FCSTD DOCUMENT  (FreeCAD 0.21R33771 (Git))
Label: Model_3
License: All rights reserved
LicenseURL: http://en.wikipedia.org/wiki/All_rights_reserved
objects: Sketcher::SketchObject×2, App::FeaturePython×2, Spreadsheet::Sheet×1, App::DocumentObjectGroupPython×1
note: 2 computed .brp shape members not serialized (recipe doc carries the construction recipe); baked Part::Feature solids carry a one-line shape summary decoded from their .brp

FEATURE [Spreadsheet::Sheet] Spreadsheet  label="Parametry"
  cells = A1='Parametry palca pacjenta, wartości proszę wpisywać w milimetrach; A3='Średnica palca pacjenta; B3='Średnica palca; C3(Srednica)=20; A4='Odległość od pierwszego więzadła do trzeciego więzadła palca pacjenta; B4='Długość paliczków; C4(Dlugosc)=60
FEATURE [Sketcher::SketchObject] Sketch  label="Model_cięcia"
  FullyConstrained = true
  expr: Constraints[103] = <<Parametry>>.Srednica
  expr: Constraints[104] = <<Parametry>>.Srednica
  expr: Constraints[105] = <<Parametry>>.Srednica
  expr: Constraints[106] = <<Parametry>>.Srednica
  expr: Constraints[107] = <<Parametry>>.Srednica / 2
  expr: Constraints[108] = <<Parametry>>.Srednica / 2
  expr: Constraints[109] = <<Parametry>>.Srednica / 2
  expr: Constraints[110] = <<Parametry>>.Srednica / 2
  expr: Constraints[12] = <<Parametry>>.Srednica
  expr: Constraints[131] = 0.5 * <<Parametry>>.Dlugosc + 0.5 * <<Parametry>>.Srednica
  expr: Constraints[132] = <<Parametry>>.Srednica / 2 + 8.5
  expr: Constraints[133] = <<Parametry>>.Srednica / 2
  expr: Constraints[134] = <<Parametry>>.Srednica / 2
  expr: Constraints[135] = <<Parametry>>.Srednica / 2
  expr: Constraints[136] = <<Parametry>>.Srednica / 2
  expr: Constraints[137] = <<Parametry>>.Srednica / 2
  expr: Constraints[138] = <<Parametry>>.Srednica / 2
  expr: Constraints[139] = <<Parametry>>.Srednica / 2
  expr: Constraints[13] = <<Parametry>>.Srednica
  expr: Constraints[140] = <<Parametry>>.Srednica / 2
  expr: Constraints[145] = 0.5 * <<Parametry>>.Dlugosc + 0.5 * <<Parametry>>.Srednica
  expr: Constraints[146] = <<Parametry>>.Srednica / 2 + 8.5
  expr: Constraints[14] = <<Parametry>>.Srednica
  expr: Constraints[15] = <<Parametry>>.Srednica
  expr: Constraints[20] = <<Parametry>>.Srednica
  expr: Constraints[21] = <<Parametry>>.Srednica
  expr: Constraints[22] = <<Parametry>>.Srednica
  expr: Constraints[23] = <<Parametry>>.Srednica
  expr: Constraints[24] = <<Parametry>>.Srednica
  expr: Constraints[25] = <<Parametry>>.Srednica
  expr: Constraints[26] = <<Parametry>>.Srednica
  expr: Constraints[27] = <<Parametry>>.Srednica
  expr: Constraints[83] = 0.5 * <<Parametry>>.Dlugosc + 0.5 * <<Parametry>>.Srednica
  expr: Constraints[84] = <<Parametry>>.Srednica / 2 + 8.5
  expr: Constraints[85] = <<Parametry>>.Srednica / 2
  expr: Constraints[86] = <<Parametry>>.Srednica / 2
  expr: Constraints[87] = <<Parametry>>.Srednica / 2
  expr: Constraints[88] = <<Parametry>>.Srednica / 2
  expr: Constraints[92] = <<Parametry>>.Dlugosc + 2 + <<Parametry>>.Srednica
  expr: Constraints[93] = <<Parametry>>.Srednica / 2 + 8.5
  expr: Constraints[94] = 0.5 * <<Parametry>>.Dlugosc + 0.5 * <<Parametry>>.Srednica
  expr: Constraints[9] = 2 * (<<Parametry>>.Srednica + 3) + 4 * 7 + 4
  sketch-geometry (56):
    g0: LineSegment StartX=0 StartY=0 StartZ=0 EndX=162 EndY=0 EndZ=0
    g1: LineSegment StartX=162 StartY=0 StartZ=0 EndX=162 EndY=78 EndZ=0
    g2: LineSegment StartX=162 StartY=78 StartZ=0 EndX=0 EndY=78 EndZ=0
    g3: LineSegment StartX=0 StartY=78 StartZ=0 EndX=0 EndY=0 EndZ=0
    g4: LineSegment StartX=30 StartY=18.5 StartZ=0 EndX=50 EndY=18.5 EndZ=0
    g5: LineSegment StartX=40 StartY=28.5 StartZ=0 EndX=40 EndY=8.5 EndZ=0
    g6: LineSegment StartX=32.9289 StartY=25.5711 StartZ=0 EndX=47.0711 EndY=11.4289 EndZ=0
    g7: LineSegment StartX=32.9289 StartY=11.4289 StartZ=0 EndX=47.0711 EndY=25.5711 EndZ=0
    g8: LineSegment StartX=30 StartY=59.5 StartZ=0 EndX=50 EndY=59.5 EndZ=0
    g9: LineSegment StartX=40 StartY=49.5 StartZ=0 EndX=40 EndY=69.5 EndZ=0
    g10: LineSegment StartX=32.9289 StartY=66.5711 StartZ=0 EndX=47.0711 EndY=52.4289 EndZ=0
    g11: LineSegment StartX=32.9289 StartY=52.4289 StartZ=0 EndX=47.0711 EndY=66.5711 EndZ=0
    g12: LineSegment StartX=112 StartY=59.5 StartZ=0 EndX=132 EndY=59.5 EndZ=0
    g13: LineSegment StartX=122 StartY=69.5 StartZ=0 EndX=122 EndY=49.5 EndZ=0
    g14: LineSegment StartX=114.929 StartY=66.5711 StartZ=0 EndX=129.071 EndY=52.4289 EndZ=0
    g15: LineSegment StartX=114.929 StartY=52.4289 StartZ=0 EndX=129.071 EndY=66.5711 EndZ=0
    g16: Circle CenterX=122 CenterY=49.5 CenterZ=0 NormalX=0 NormalY=0 NormalZ=1 AngleXU=0 Radius=0.25
    g17: Circle CenterX=114.929 CenterY=52.4289 CenterZ=0 NormalX=0 NormalY=0 NormalZ=1 AngleXU=0 Radius=0.25
    g18: Circle CenterX=112 CenterY=59.5 CenterZ=0 NormalX=0 NormalY=0 NormalZ=1 AngleXU=0 Radius=0.25
    g19: Circle CenterX=114.929 CenterY=66.5711 CenterZ=0 NormalX=0 NormalY=0 NormalZ=1 AngleXU=0 Radius=0.25
    g20: Circle CenterX=122 CenterY=69.5 CenterZ=0 NormalX=0 NormalY=0 NormalZ=1 AngleXU=0 Radius=0.25
    g21: Circle CenterX=129.071 CenterY=66.5711 CenterZ=0 NormalX=0 NormalY=0 NormalZ=1 AngleXU=0 Radius=0.25
    g22: Circle CenterX=132 CenterY=59.5 CenterZ=0 NormalX=0 NormalY=0 NormalZ=1 AngleXU=0 Radius=0.25
    g23: Circle CenterX=129.071 CenterY=52.4289 CenterZ=0 NormalX=0 NormalY=0 NormalZ=1 AngleXU=0 Radius=0.25
    g24: Circle CenterX=40 CenterY=69.5 CenterZ=0 NormalX=0 NormalY=0 NormalZ=1 AngleXU=0 Radius=0.25
    g25: Circle CenterX=47.0711 CenterY=66.5711 CenterZ=0 NormalX=0 NormalY=0 NormalZ=1 AngleXU=0 Radius=0.25
    g26: Circle CenterX=50 CenterY=59.5 CenterZ=0 NormalX=0 NormalY=0 NormalZ=1 AngleXU=0 Radius=0.25
    g27: Circle CenterX=47.0711 CenterY=52.4289 CenterZ=0 NormalX=0 NormalY=0 NormalZ=1 AngleXU=0 Radius=0.25
    g28: Circle CenterX=40 CenterY=49.5 CenterZ=0 NormalX=0 NormalY=0 NormalZ=1 AngleXU=0 Radius=0.25
    g29: Circle CenterX=32.9289 CenterY=52.4289 CenterZ=0 NormalX=0 NormalY=0 NormalZ=1 AngleXU=0 Radius=0.25
    g30: Circle CenterX=30 CenterY=59.5 CenterZ=0 NormalX=0 NormalY=0 NormalZ=1 AngleXU=0 Radius=0.25
    g31: Circle CenterX=32.9289 CenterY=66.5711 CenterZ=0 NormalX=0 NormalY=0 NormalZ=1 AngleXU=0 Radius=0.25
    g32: Circle CenterX=32.9289 CenterY=25.5711 CenterZ=0 NormalX=0 NormalY=0 NormalZ=1 AngleXU=0 Radius=0.25
    g33: Circle CenterX=30 CenterY=18.5 CenterZ=0 NormalX=0 NormalY=0 NormalZ=1 AngleXU=0 Radius=0.25
    g34: Circle CenterX=32.9289 CenterY=11.4289 CenterZ=0 NormalX=0 NormalY=0 NormalZ=1 AngleXU=0 Radius=0.25
    g35: Circle CenterX=47.0711 CenterY=11.4289 CenterZ=0 NormalX=0 NormalY=0 NormalZ=1 AngleXU=0 Radius=0.25
    g36: Circle CenterX=50 CenterY=18.5 CenterZ=0 NormalX=0 NormalY=0 NormalZ=1 AngleXU=0 Radius=0.25
    g37: Circle CenterX=47.0711 CenterY=25.5711 CenterZ=0 NormalX=0 NormalY=0 NormalZ=1 AngleXU=0 Radius=0.25
    g38: Circle CenterX=40 CenterY=8.5 CenterZ=0 NormalX=0 NormalY=0 NormalZ=1 AngleXU=0 Radius=0.25
    g39: Circle CenterX=40 CenterY=28.5 CenterZ=0 NormalX=0 NormalY=0 NormalZ=1 AngleXU=0 Radius=0.25
    g40: GeomPoint X=40 Y=18.5 Z=0
    g41: GeomPoint X=122 Y=18.5 Z=0
    g42: LineSegment StartX=114.929 StartY=11.4289 StartZ=0 EndX=129.071 EndY=25.5711 EndZ=0
    g43: LineSegment StartX=114.929 StartY=25.5711 StartZ=0 EndX=129.071 EndY=11.4289 EndZ=0
    g44: LineSegment StartX=122 StartY=28.5 StartZ=0 EndX=122 EndY=8.5 EndZ=0
    g45: LineSegment StartX=112 StartY=18.5 StartZ=0 EndX=132 EndY=18.5 EndZ=0
    g46: Circle CenterX=122 CenterY=28.5 CenterZ=0 NormalX=0 NormalY=0 NormalZ=1 AngleXU=0 Radius=0.25
    g47: Circle CenterX=129.071 CenterY=25.5711 CenterZ=0 NormalX=0 NormalY=0 NormalZ=1 AngleXU=0 Radius=0.25
    g48: Circle CenterX=132 CenterY=18.5 CenterZ=0 NormalX=0 NormalY=0 NormalZ=1 AngleXU=0 Radius=0.25
    g49: Circle CenterX=129.071 CenterY=11.4289 CenterZ=0 NormalX=0 NormalY=0 NormalZ=1 AngleXU=0 Radius=0.25
    g50: Circle CenterX=114.929 CenterY=11.4289 CenterZ=0 NormalX=0 NormalY=0 NormalZ=1 AngleXU=0 Radius=0.25
    g51: Circle CenterX=112 CenterY=18.5 CenterZ=0 NormalX=0 NormalY=0 NormalZ=1 AngleXU=0 Radius=0.25
    g52: Circle CenterX=114.929 CenterY=25.5711 CenterZ=0 NormalX=0 NormalY=0 NormalZ=1 AngleXU=0 Radius=0.25
    g53: Circle CenterX=122 CenterY=8.5 CenterZ=0 NormalX=0 NormalY=0 NormalZ=1 AngleXU=0 Radius=0.25
    g54: GeomPoint X=122 Y=59.5 Z=0
    g55: GeomPoint X=40 Y=59.5 Z=0
  constraints (147):
    c: Coincident(g0,g1)
    c: Coincident(g1,g2)
    c: Coincident(g2,g3)
    c: Coincident(g3,g0)
    c: Horizontal(g0)
    c: Horizontal(g2)
    c: Vertical(g1)
    c: Vertical(g3)
    c: Coincident(g0,g-1)
    c: DistanceY(g1,g1) = 78
    c: Horizontal(g4)
    c: Vertical(g5)
    c: DistanceX(g4,g4) = 20
    c: Distance(g7) = 20
    c: Distance(g5) = 20
    c: Distance(g6) = 20
    c: Angle(g4,g7) = 0.785398
    c: Angle(g6,g4) = 0.785398
    c: Horizontal(g8)
    c: Vertical(g9)
    c: Distance(g8) = 20
    c: Distance(g10) = 20
    c: Distance(g9) = 20
    c: Distance(g11) = 20
    c: Distance(g12) = 20
    c: Distance(g15) = 20
    c: Distance(g13) = 20
    c: Distance(g14) = 20
    c: Angle(g8,g11) = 0.785398
    c: Angle(g9,g10) = 0.785398
    c: Angle(g2,g12) = 0
    c: Angle(g2,g13) = 1.5708
    c: Angle(g12,g15) = 0.785398
    c: Angle(g14,g12) = 0.785398
    c: Coincident(g16,g13)
    c: Coincident(g17,g15)
    c: Coincident(g18,g12)
    c: Coincident(g19,g14)
    c: Coincident(g20,g13)
    c: Coincident(g21,g15)
    c: Coincident(g22,g12)
    c: Coincident(g23,g14)
    c: Coincident(g24,g9)
    c: Coincident(g25,g11)
    c: Coincident(g26,g8)
    c: Coincident(g27,g10)
    c: Coincident(g28,g9)
    c: Coincident(g29,g11)
    c: Coincident(g30,g8)
    c: Coincident(g31,g10)
    c: Coincident(g32,g6)
    c: Coincident(g33,g4)
    c: Coincident(g34,g7)
    c: Coincident(g35,g6)
    c: Coincident(g36,g4)
    c: Coincident(g37,g7)
    c: Coincident(g38,g5)
    c: Diameter(g30) = 0.5
    c: Diameter(g31) = 0.5
    c: Diameter(g24) = 0.5
    c: Diameter(g25) = 0.5
    c: Diameter(g26) = 0.5
    c: Diameter(g27) = 0.5
    c: Diameter(g28) = 0.5
    c: Diameter(g19) = 0.5
    c: Diameter(g20) = 0.5
    c: Diameter(g21) = 0.5
    c: Diameter(g22) = 0.5
    c: Diameter(g23) = 0.5
    c: Diameter(g16) = 0.5
    c: Diameter(g17) = 0.5
    c: Diameter(g18) = 0.5
    c: Diameter(g38) = 0.5
    c: Diameter(g35) = 0.5
    c: Diameter(g36) = 0.5
    c: Diameter(g37) = 0.5
    c: Diameter(g32) = 0.5
    c: Diameter(g33) = 0.5
    c: Diameter(g34) = 0.5
    c: Diameter(g29) = 0.5
    c: Coincident(g39,g5)
    c: Diameter(g39) = 0.5
    c: PointOnObject(g40,g4)
    c: DistanceX(g0,g40) = 40
    c: DistanceY(g0,g40) = 18.5
    c: Distance(g40,g4) = 10
    c: Distance(g40,g7) = 10
    c: Distance(g40,g6) = 10
    c: Distance(g40,g5) = 10
    c: PointOnObject(g40,g7)
    c: PointOnObject(g40,g6)
    c: PointOnObject(g40,g5)
    c: DistanceX(g40,g41) = 82
    c: DistanceY(g0,g41) = 18.5
    c: DistanceX(g41,g0) = 40
    c: PointOnObject(g41,g43)
    c: PointOnObject(g41,g42)
    c: PointOnObject(g41,g45)
    c: PointOnObject(g41,g44)
    c: Angle(g0,g45) = 0
    c: Angle(g44,g0) = 1.5708
    c: Angle(g42,g44) = 0.785398
    c: Angle(g44,g43) = 0.785398
    c: Distance(g43) = 20
    c: Distance(g42) = 20
    c: Distance(g44) = 20
    c: Distance(g45) = 20
    c: Distance(g41,g45) = 10
    c: Distance(g41,g42) = 10
    c: Distance(g41,g44) = 10
    c: Distance(g41,g43) = 10
    c: Coincident(g46,g44)
    c: Coincident(g47,g42)
    c: Coincident(g48,g45)
    c: Coincident(g49,g43)
    c: Coincident(g50,g42)
    c: Coincident(g51,g45)
    c: Coincident(g52,g43)
    c: Coincident(g53,g44)
    c: Diameter(g52) = 0.5
    c: Diameter(g46) = 0.5
    c: Diameter(g47) = 0.5
    c: Diameter(g48) = 0.5
    c: Diameter(g49) = 0.5
    c: Diameter(g53) = 0.5
    c: Diameter(g50) = 0.5
    c: Diameter(g51) = 0.5
    c: PointOnObject(g54,g13)
    c: PointOnObject(g54,g15)
    c: PointOnObject(g54,g12)
    c: PointOnObject(g54,g14)
    c: DistanceX(g54,g1) = 40
    c: DistanceY(g54,g1) = 18.5
    c: Distance(g54,g13) = 10
    c: Distance(g54,g15) = 10
    c: Distance(g54,g12) = 10
    c: Distance(g54,g14) = 10
    c: Distance(g55,g9) = 10
    c: Distance(g55,g11) = 10
    c: Distance(g55,g8) = 10
    c: Distance(g55,g10) = 10
    c: PointOnObject(g55,g10)
    c: PointOnObject(g55,g9)
    c: PointOnObject(g55,g11)
    c: PointOnObject(g55,g8)
    c: DistanceX(g2,g55) = 40
    c: DistanceY(g55,g2) = 18.5
FEATURE [App::FeaturePython] Layer  label="Cięcie laserem"  # WARN: FeaturePython — macro-defined, semantics opaque (R4)
  Group = -> [Sketch]
FEATURE [Sketcher::SketchObject] Sketch001  label="Model_zgrzewania"
  FullyConstrained = true
  expr: Constraints[10] = <<Parametry>>.Dlugosc + 2 + <<Parametry>>.Srednica
  expr: Constraints[11] = <<Parametry>>.Srednica / 2 + 8.5
  expr: Constraints[12] = <<Parametry>>.Srednica / 2 + 8.5
  expr: Constraints[13] = (2 * (<<Parametry>>.Srednica + 3) + 4 * 7 + 4) * 0.5
  expr: Constraints[14] = (2 * (<<Parametry>>.Srednica + 3) + 4 * 7 + 4) * 0.5
  expr: Constraints[15] = <<Parametry>>.Dlugosc + 2 + <<Parametry>>.Srednica + 2 * (0.5 * <<Parametry>>.Dlugosc + 0.5 * <<Parametry>>.Srednica) - 2
  expr: Constraints[5] = <<Parametry>>.Srednica + 5
  expr: Constraints[6] = <<Parametry>>.Srednica + 5
  expr: Constraints[9] = 0.5 * <<Parametry>>.Dlugosc + 0.5 * <<Parametry>>.Srednica
  sketch-geometry (5):
    g0: LineSegment StartX=160 StartY=39 StartZ=0 EndX=160 EndY=2 EndZ=0
    g1: LineSegment StartX=160 StartY=2 StartZ=0 EndX=2 EndY=2 EndZ=0
    g2: LineSegment StartX=2 StartY=2 StartZ=0 EndX=2 EndY=39 EndZ=0
    g3: Circle CenterX=40 CenterY=18.5 CenterZ=0 NormalX=0 NormalY=0 NormalZ=1 AngleXU=0 Radius=12.5
    g4: Circle CenterX=122 CenterY=18.5 CenterZ=0 NormalX=0 NormalY=0 NormalZ=1 AngleXU=0 Radius=12.5
  constraints (16):
    c: Coincident(g0,g1)
    c: Coincident(g1,g2)
    c: Horizontal(g1)
    c: Vertical(g0)
    c: Vertical(g2)
    c: Diameter(g4) = 25
    c: Diameter(g3) = 25
    c: DistanceY(g-1,g1) = 2
    c: DistanceX(g-1,g1) = 2
    c: DistanceX(g-1,g3) = 40
    c: DistanceX(g3,g4) = 82
    c: DistanceY(g-1,g3) = 18.5
    c: DistanceY(g-1,g4) = 18.5
    c: DistanceY(g-1,g2) = 39
    c: DistanceY(g-1,g0) = 39
    c: DistanceX(g-1,g0) = 160
FEATURE [App::FeaturePython] Layer001  label="Zgrzewanie"  # WARN: FeaturePython — macro-defined, semantics opaque (R4)
  Group = -> [Sketch001]
FEATURE [App::DocumentObjectGroupPython] LayerContainer  label="Warstwy"  # scripted group (container) (typed FeaturePython)
  Group = -> [Layer,Layer001]
